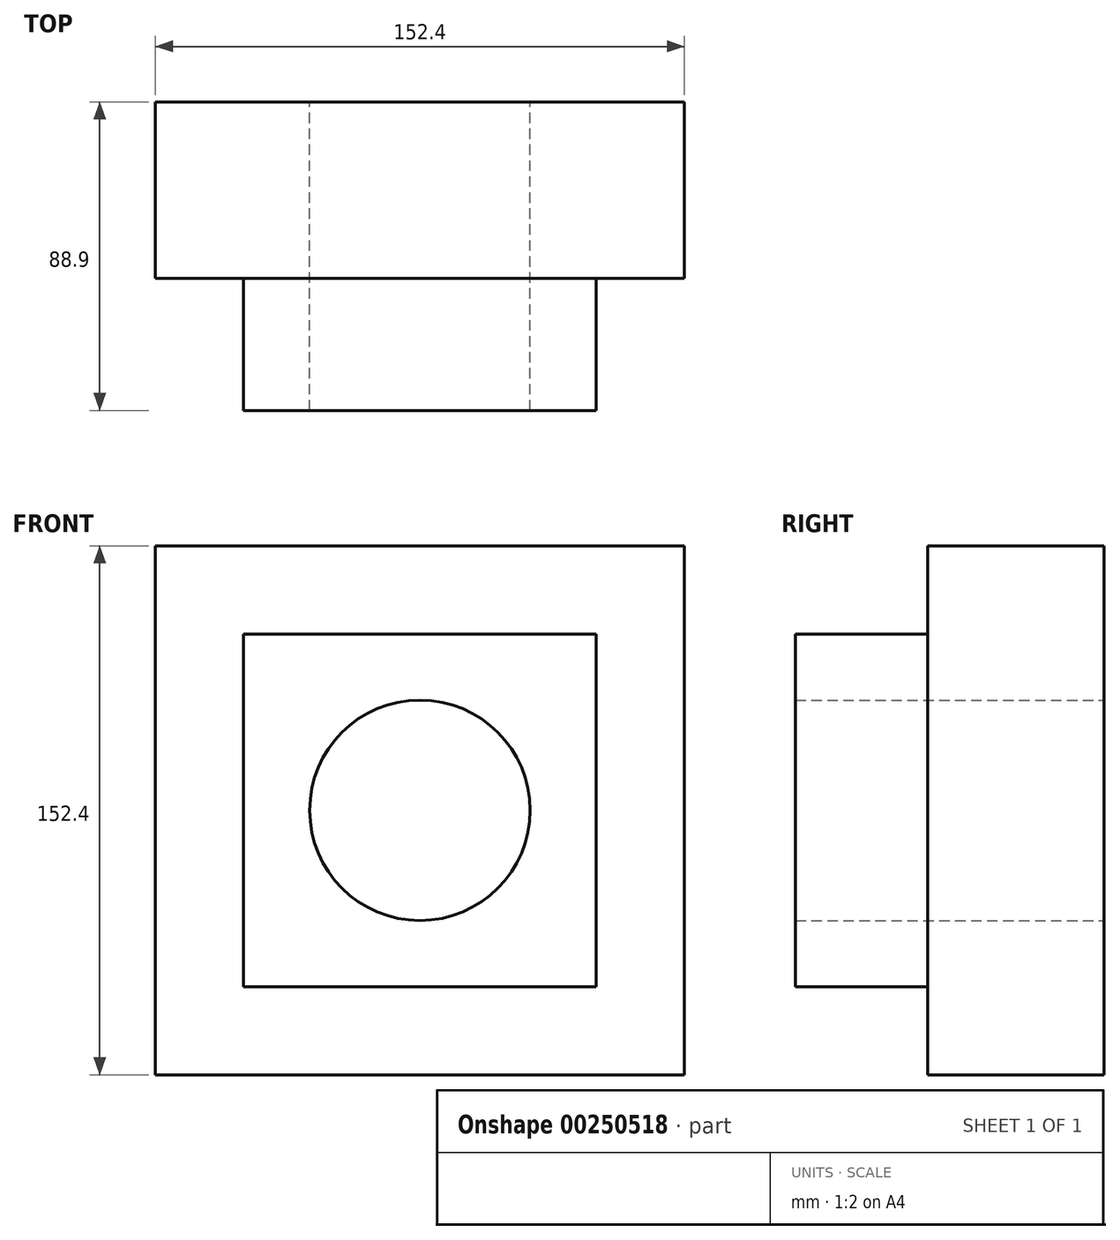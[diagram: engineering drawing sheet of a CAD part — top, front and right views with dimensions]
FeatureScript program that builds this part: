
annotation { "Feature Type Name" : "Feature", "Feature Type Description" : "" }
export const myFeature = defineFeature(function(context is Context, id is Id, definition is map)
    precondition{}
    {
        {
            var Q0;
            Q0=qCreatedBy(makeId("Front.planeOp"),FACE);
            var sketch = newSketch(context, id + "F0", { "sketchPlane" : qUnion([Q0])});
            skCircle(sketch, "E0", {"center": v(0, 0) * mm, "radius": 31.75 * mm});
            skLineSegment(sketch, "E1.bottom", {"start": v(50.8, -50.8) * mm, "end": v(-50.8, -50.8) * mm});
            skLineSegment(sketch, "E1.top", {"start": v(50.8, 50.8) * mm, "end": v(-50.8, 50.8) * mm});
            skLineSegment(sketch, "E1.left", {"start": v(50.8, -50.8) * mm, "end": v(50.8, 50.8) * mm});
            skLineSegment(sketch, "E1.right", {"start": v(-50.8, -50.8) * mm, "end": v(-50.8, 50.8) * mm});
            skLineSegment(sketch, "E2.bottom", {"start": v(76.2, -76.2) * mm, "end": v(-76.2, -76.2) * mm});
            skLineSegment(sketch, "E2.top", {"start": v(76.2, 76.2) * mm, "end": v(-76.2, 76.2) * mm});
            skLineSegment(sketch, "E2.left", {"start": v(76.2, -76.2) * mm, "end": v(76.2, 76.2) * mm});
            skLineSegment(sketch, "E2.right", {"start": v(-76.2, -76.2) * mm, "end": v(-76.2, 76.2) * mm});
            skSolve(sketch);
        }
        {
            var Q0;
            Q0=makeQuery(id+"F0.imprint","IMPRINT",FACE,{"disambiguationData":[TD([[makeQuery(id+"F0.imprint","IMPRINT",EDGE,{"derivedFrom":sQuery(id+"F0.wireOp",EDGE,"E0")}),-1.0]])]});
            extrude(context, id + "F1", {"entities" : qUnion([Q0]), "depth" : 38.1 * mm});
        }
        {
            var Q0;
            Q0=makeQuery(id+"F0.imprint","IMPRINT",FACE,{"disambiguationData":[TD([[makeQuery(id+"F0.imprint","IMPRINT",EDGE,{"derivedFrom":sQuery(id+"F0.wireOp",EDGE,"E1.bottom")}),1.0]])]});
            var Q1;
            Q1=makeQuery(id+"F0.imprint","IMPRINT",FACE,{"disambiguationData":[TD([[makeQuery(id+"F0.imprint","IMPRINT",EDGE,{"derivedFrom":sQuery(id+"F0.wireOp",EDGE,"E0")}),-1.0]])]});
            extrude(context, id + "F2", {"entities" : qUnion([Q0, Q1]), "operationType" : NewBodyOperationType.ADD, "oppositeDirection" : true, "depth" : 50.8 * mm});
        }
    });
